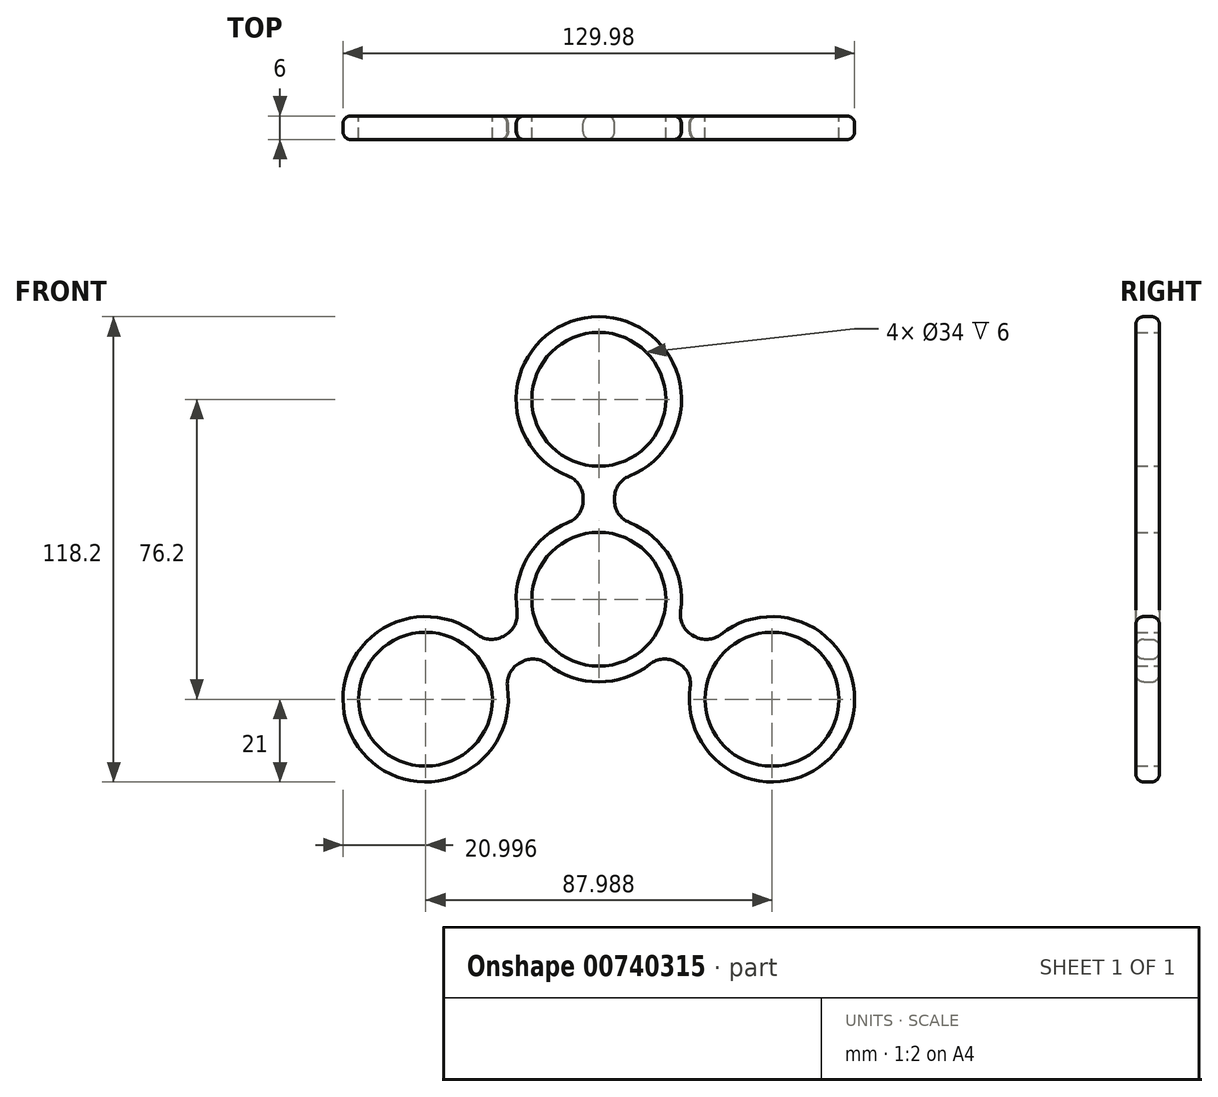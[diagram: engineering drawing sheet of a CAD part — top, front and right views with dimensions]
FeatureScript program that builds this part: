
annotation { "Feature Type Name" : "Feature", "Feature Type Description" : "" }
export const myFeature = defineFeature(function(context is Context, id is Id, definition is map)
    precondition{}
    {
        {
            var Q0;
            Q0=qCreatedBy(makeId("Front.planeOp"),FACE);
            var sketch = newSketch(context, id + "F0", { "sketchPlane" : qUnion([Q0])});
            skCircle(sketch, "E0", {"center": v(0, 0) * mm, "radius": 17 * mm});
            skArc(sketch, "E1.0", {"start": v(-7.78, 19.5) * mm, "mid": v(-18.19, 10.5) * mm, "end": v(-20.78, -3.02) * mm});
            skCircle(sketch, "E2", {"center": v(0, 50.8) * mm, "radius": 17 * mm});
            skArc(sketch, "E3.0", {"start": v(7.78, 31.3) * mm, "mid": v(0, 71.8) * mm, "end": v(-7.78, 31.3) * mm});
            skArc(sketch, "E4.1.0", {"start": v(-30.99, -8.91) * mm, "mid": v(-62.18, -35.9) * mm, "end": v(-23.21, -22.38) * mm});
            skCircle(sketch, "E4.1.1", {"center": v(-44, -25.4) * mm, "radius": 17 * mm});
            skArc(sketch, "E4.2.0", {"start": v(24.14, -18.56) * mm, "mid": v(62.18, -35.9) * mm, "end": v(28.14, -11.63) * mm});
            skCircle(sketch, "E4.2.1", {"center": v(44, -25.4) * mm, "radius": 17 * mm});
            skLineSegment(sketch, "E5", {"start": v(0, 50.8) * mm, "end": v(0, 0) * mm, "construction": true});
            skLineSegment(sketch, "E6", {"start": v(-4, 25.72) * mm, "end": v(-4, 25.08) * mm});
            skLineSegment(sketch, "E7.MirrorCS", {"start": v(4, 25.72) * mm, "end": v(4, 25.08) * mm});
            skPoint(sketch, "E8.visualSharp", {"position": v(-4, 30.18) * mm});
            skArc(sketch, "E8.filletArc", {"start": v(-4, 25.72) * mm, "mid": v(-5.03, 29.09) * mm, "end": v(-7.78, 31.3) * mm});
            skPoint(sketch, "E9.visualSharp", {"position": v(4, 30.18) * mm});
            skArc(sketch, "E9.filletArc", {"start": v(7.78, 31.3) * mm, "mid": v(5.03, 29.09) * mm, "end": v(4, 25.72) * mm});
            skPoint(sketch, "E10.visualSharp", {"position": v(-4, 20.62) * mm});
            skArc(sketch, "E10.filletArc", {"start": v(-7.78, 19.5) * mm, "mid": v(-5.03, 21.71) * mm, "end": v(-4, 25.08) * mm});
            skPoint(sketch, "E11.visualSharp", {"position": v(4, 20.62) * mm});
            skArc(sketch, "E11.filletArc", {"start": v(4, 25.08) * mm, "mid": v(5.03, 21.71) * mm, "end": v(7.78, 19.5) * mm});
            skPoint(sketch, "E12.1.0", {"position": v(-28.14, -11.63) * mm});
            skPoint(sketch, "E12.1.1", {"position": v(-19.85, -6.84) * mm});
            skPoint(sketch, "E12.1.2", {"position": v(-24.14, -18.56) * mm});
            skPoint(sketch, "E12.1.3", {"position": v(-15.85, -13.77) * mm});
            skArc(sketch, "E12.1.4", {"start": v(-30.99, -8.91) * mm, "mid": v(-27.7, -10.18) * mm, "end": v(-24.27, -9.4) * mm});
            skArc(sketch, "E12.1.5", {"start": v(-20.27, -16.32) * mm, "mid": v(-22.67, -18.9) * mm, "end": v(-23.21, -22.38) * mm});
            skArc(sketch, "E12.1.6", {"start": v(-13, -16.49) * mm, "mid": v(-16.29, -15.22) * mm, "end": v(-19.72, -16) * mm});
            skArc(sketch, "E12.1.7", {"start": v(-23.72, -9.08) * mm, "mid": v(-21.32, -6.5) * mm, "end": v(-20.78, -3.02) * mm});
            skLineSegment(sketch, "E12.1.8", {"start": v(-20.27, -16.32) * mm, "end": v(-19.72, -16) * mm});
            skLineSegment(sketch, "E12.1.9", {"start": v(-24.27, -9.4) * mm, "end": v(-23.72, -9.08) * mm});
            skPoint(sketch, "E12.2.0", {"position": v(24.14, -18.56) * mm});
            skPoint(sketch, "E12.2.1", {"position": v(15.85, -13.77) * mm});
            skPoint(sketch, "E12.2.2", {"position": v(28.14, -11.63) * mm});
            skPoint(sketch, "E12.2.3", {"position": v(19.85, -6.84) * mm});
            skArc(sketch, "E12.2.4", {"start": v(23.21, -22.38) * mm, "mid": v(22.67, -18.9) * mm, "end": v(20.27, -16.32) * mm});
            skArc(sketch, "E12.2.5", {"start": v(24.27, -9.4) * mm, "mid": v(27.7, -10.18) * mm, "end": v(30.99, -8.91) * mm});
            skArc(sketch, "E12.2.6", {"start": v(20.78, -3.02) * mm, "mid": v(21.32, -6.5) * mm, "end": v(23.72, -9.08) * mm});
            skArc(sketch, "E12.2.7", {"start": v(19.72, -16) * mm, "mid": v(16.29, -15.22) * mm, "end": v(13, -16.49) * mm});
            skLineSegment(sketch, "E12.2.8", {"start": v(24.27, -9.4) * mm, "end": v(23.72, -9.08) * mm});
            skLineSegment(sketch, "E12.2.9", {"start": v(20.27, -16.32) * mm, "end": v(19.72, -16) * mm});
            skArc(sketch, "E13.trimOffspring", {"start": v(-13, -16.49) * mm, "mid": v(0, -21) * mm, "end": v(13, -16.49) * mm});
            skArc(sketch, "E14.trimOffspring", {"start": v(20.78, -3.02) * mm, "mid": v(18.19, 10.5) * mm, "end": v(7.78, 19.5) * mm});
            skSolve(sketch);
        }
        {
            var Q0;
            Q0=makeQuery(id+"F0.imprint","IMPRINT",FACE,{"disambiguationData":[TD([[makeQuery(id+"F0.imprint","IMPRINT",EDGE,{"derivedFrom":sQuery(id+"F0.wireOp",EDGE,"E0")}),-1.0]])]});
            extrude(context, id + "F1", {"entities" : qUnion([Q0]), "endBound" : BoundingType.SYMMETRIC, "depth" : 6 * mm, "offsetDistance" : 25.4 * mm});
        }
        {
            var Q0;
            Q0=makeQuery(id+"F1.opExtrude","CAP_EDGE",EDGE,{"disambiguationData":[OSD([sQuery(id+"F0.wireOp",EDGE,"E3.0")])],"isStart":true});
            var Q1;
            Q1=makeQuery(id+"F1.opExtrude","SWEPT_FACE",FACE,{"disambiguationData":[OSD([sQuery(id+"F0.wireOp",EDGE,"E9.filletArc")])]});
            var Q2;
            Q2=makeQuery(id+"F1.opExtrude","SWEPT_EDGE",EDGE,{"disambiguationData":[OSD([sQuery(id+"F0.wireOp",EDGE,"E7.MirrorCS"),sQuery(id+"F0.wireOp",EDGE,"E11.filletArc")])]});
            var Q3;
            Q3=makeQuery(id+"F1.opExtrude","SWEPT_FACE",FACE,{"disambiguationData":[OSD([sQuery(id+"F0.wireOp",EDGE,"E11.filletArc")])]});
            var Q4;
            Q4=makeQuery(id+"F1.opExtrude","SWEPT_EDGE",EDGE,{"disambiguationData":[OSD([sQuery(id+"F0.wireOp",EDGE,"E12.2.6"),sQuery(id+"F0.wireOp",EDGE,"E14.trimOffspring")])]});
            var Q5;
            Q5=makeQuery(id+"F1.opExtrude","CAP_EDGE",EDGE,{"disambiguationData":[OSD([sQuery(id+"F0.wireOp",EDGE,"E12.2.6")])],"isStart":true});
            fillet(context, id + "F2", {"entities" : qUnion([Q0, Q1, Q2, Q3, Q4, Q5]), "radius" : 2 * mm, "tangentPropagation" : true, "allowEdgeOverflow" : false});
        }
    });
